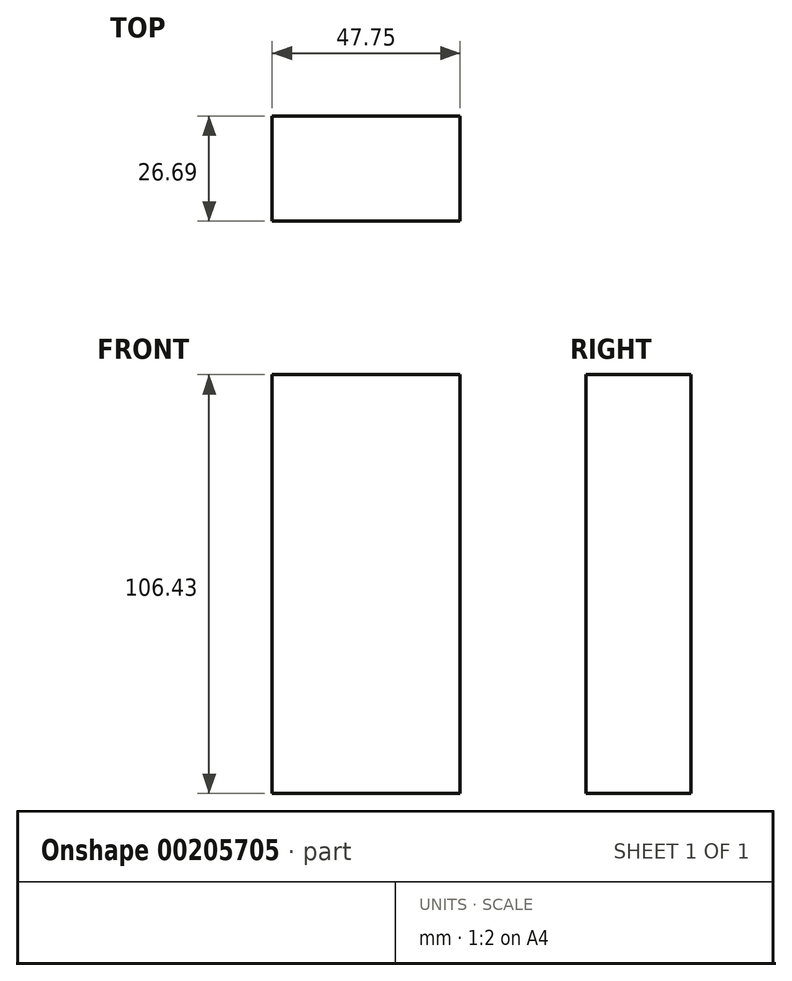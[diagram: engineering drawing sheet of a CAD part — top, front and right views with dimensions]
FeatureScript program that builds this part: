
annotation { "Feature Type Name" : "Feature", "Feature Type Description" : "" }
export const myFeature = defineFeature(function(context is Context, id is Id, definition is map)
    precondition{}
    {
        {
            var Q0;
            Q0=qCreatedBy(makeId("Top.planeOp"),FACE);
            var sketch = newSketch(context, id + "F0", { "sketchPlane" : qUnion([Q0])});
            skLineSegment(sketch, "E0.bottom", {"start": v(-47.75, 26.7) * mm, "end": v(0, 26.7) * mm});
            skLineSegment(sketch, "E0.top", {"start": v(-47.75, 0) * mm, "end": v(0, 0) * mm});
            skLineSegment(sketch, "E0.left", {"start": v(-47.75, 26.7) * mm, "end": v(-47.75, 0) * mm});
            skLineSegment(sketch, "E0.right", {"start": v(0, 26.7) * mm, "end": v(0, 0) * mm});
            skSolve(sketch);
        }
        {
            var Q0;
            Q0=makeQuery(id+"F0.imprint","IMPRINT",FACE,{"disambiguationData":[TD([[makeQuery(id+"F0.imprint","IMPRINT",EDGE,{"derivedFrom":sQuery(id+"F0.wireOp",EDGE,"E0.bottom")}),-1.0]])]});
            extrude(context, id + "F1", {"entities" : qUnion([Q0]), "endBound" : BoundingType.SYMMETRIC, "depth" : 63 * mm, "hasSecondDirection" : true, "secondDirectionOppositeDirection" : false, "secondDirectionDepth" : 2.8 * mm});
        }
        {
            var Q0;
            Q0=makeQuery(id+"F1.opExtrude","CAP_FACE",FACE,{"disambiguationData":[OSD([sQuery(id+"F0.wireOp",EDGE,"E0.bottom"),sQuery(id+"F0.wireOp",EDGE,"E0.top"),sQuery(id+"F0.wireOp",EDGE,"E0.left"),sQuery(id+"F0.wireOp",EDGE,"E0.right")])],"isStart":false});
            extrude(context, id + "F2", {"entities" : qUnion([Q0]), "operationType" : NewBodyOperationType.ADD, "depth" : 43.43 * mm});
        }
    });
